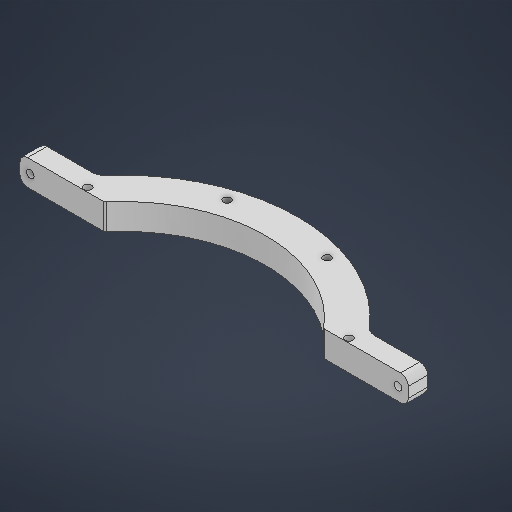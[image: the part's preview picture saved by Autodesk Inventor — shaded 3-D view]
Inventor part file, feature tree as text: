
AUTODESK INVENTOR PART (.ipt)
format: ipt  version: 2025 (Build 290162000, 162)  size: 303,616 bytes
history: native  units: in
note: dims shown in document units (in); Inventor stores cm internally (conversion verified against a paired STEP export)
features: sketch x6, fillet x4, extrude x3, hole x2, mirror x2, projected_geometry x1
ambient origin geometry x8: Origin, YZ Plane, XZ Plane, XY Plane, X Axis, Y Axis, Z Axis, Center Point
bodies: Solid1 (feature_tree)
feature tree (18):
  extrude  "Extrusion1"  Depth=8.6614in
  extrude  "Extrusion3"  Depth=0.7874in
  fillet  "Fillet1"  Radius=0.9843in
  fillet  "Fillet2"  Radius=0.5906in
  fillet  "Fillet3"  Radius=0.7874in
  hole  "Hole2"  [1 undecoded]
  mirror  "Mirror1"
  mirror  "Mirror2"
  hole  "Hole3"  [1 undecoded]
  extrude  "Extrusion7"  Depth=0.2362in
  fillet  "Fillet7"  Radius=0.3937in
  sketch  "Sketch1"  dims[d0=10.6299in d1=8.6614in]
  sketch  "Sketch4"  dims[d25=0.5906in d26=0.0in d27=0.0in]
  projected_geometry  "Projected Loop1"
  sketch  "Sketch5"  dims[d28=0.2362in d29=0.3937in]
  sketch  "Sketch7"  dims[d30=0.0787in]
  sketch  "Sketch11"  dims[d31=0.2362in d32=0.2362in d33=0.3543in d34=0.1969in d35=90.0deg d36=0.315in d37=0.8108in d38=0.315in d39=0.3937in d43=0.1969in d44=0.2362in d45=0.1575in d46=0.0787in d47=90.0deg d48=0.315in d49=0.8108in d50=5.0197in d57=0.3937in d61=0.0in d62=0.0in d63=0.0787in d69=9.8425in d75=0.2362in d76=3.937in d78=360.0deg]
  sketch  "Sketch Circular Pattern3"  dims[d2=0.7874in d3=0.0in d21=3.9469in d22=0.9843in d23=0.5906in d24=0.7874in]
note: 2 required parameter values undecoded (feature->parameter linkage not recoverable at this tier; creation-order binding heuristic only, values carry confidence <= 0.55)
